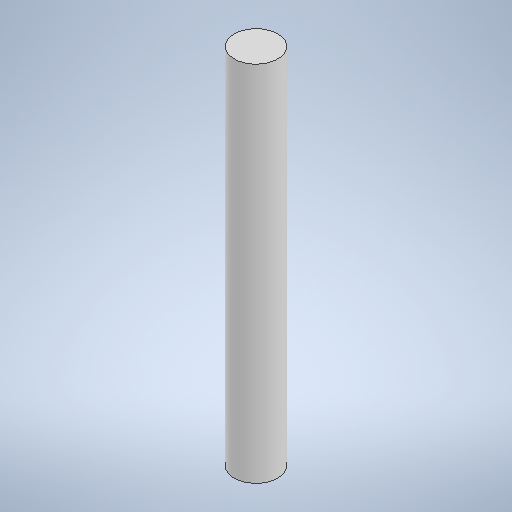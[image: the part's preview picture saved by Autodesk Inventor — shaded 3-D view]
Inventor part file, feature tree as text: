
AUTODESK INVENTOR PART (.ipt)
format: ipt  version: 2025.1 (Build 291241000, 241)  size: 221,696 bytes
history: native  units: mm
features: extrude x1, sketch x1
ambient origin geometry x8: Origin, YZ Plane, XZ Plane, XY Plane, X Axis, Y Axis, Z Axis, Center Point
bodies: Solide1 (feature_tree)
feature tree (2):
  extrude  "Extrusion1"  Depth=3.0mm
  sketch  "Esquisse1"
